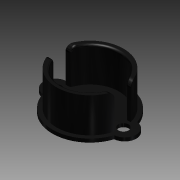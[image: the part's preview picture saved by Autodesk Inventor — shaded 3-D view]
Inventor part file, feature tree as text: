
AUTODESK INVENTOR PART (.ipt)
format: ipt  version: 2014 (Build 180170000, 170)  size: 176,640 bytes
history: native  units: in
note: dims shown in document units (in); Inventor stores cm internally (conversion verified against a paired STEP export)
features: sketch x3, extrude x2, fillet x2
ambient origin geometry x8: Origin, YZ Plane, XZ Plane, XY Plane, X Axis, Y Axis, Z Axis, Center Point
bodies: Solid1 (feature_tree)
feature tree (7):
  extrude  "Extrusion1"  Depth=0.1in
  sketch  "Sketch2"  dims[d16=0.1in d17=0.1in d18=0.5in d19=0.03in d20=0.0in]
  extrude  "Extrusion2"  Depth=0.1in
  fillet  "Fillet1"  Radius=0.5in
  fillet  "Fillet2"  Radius=0.03in
  sketch  "Sketch1"  dims[d2=0.09in d15=0.1in]
  sketch  "Sketch3"  dims[d21=0.5in d22=0.58in d26=0.3in d27=0.0in d28=0.05in d29=0.02in]
